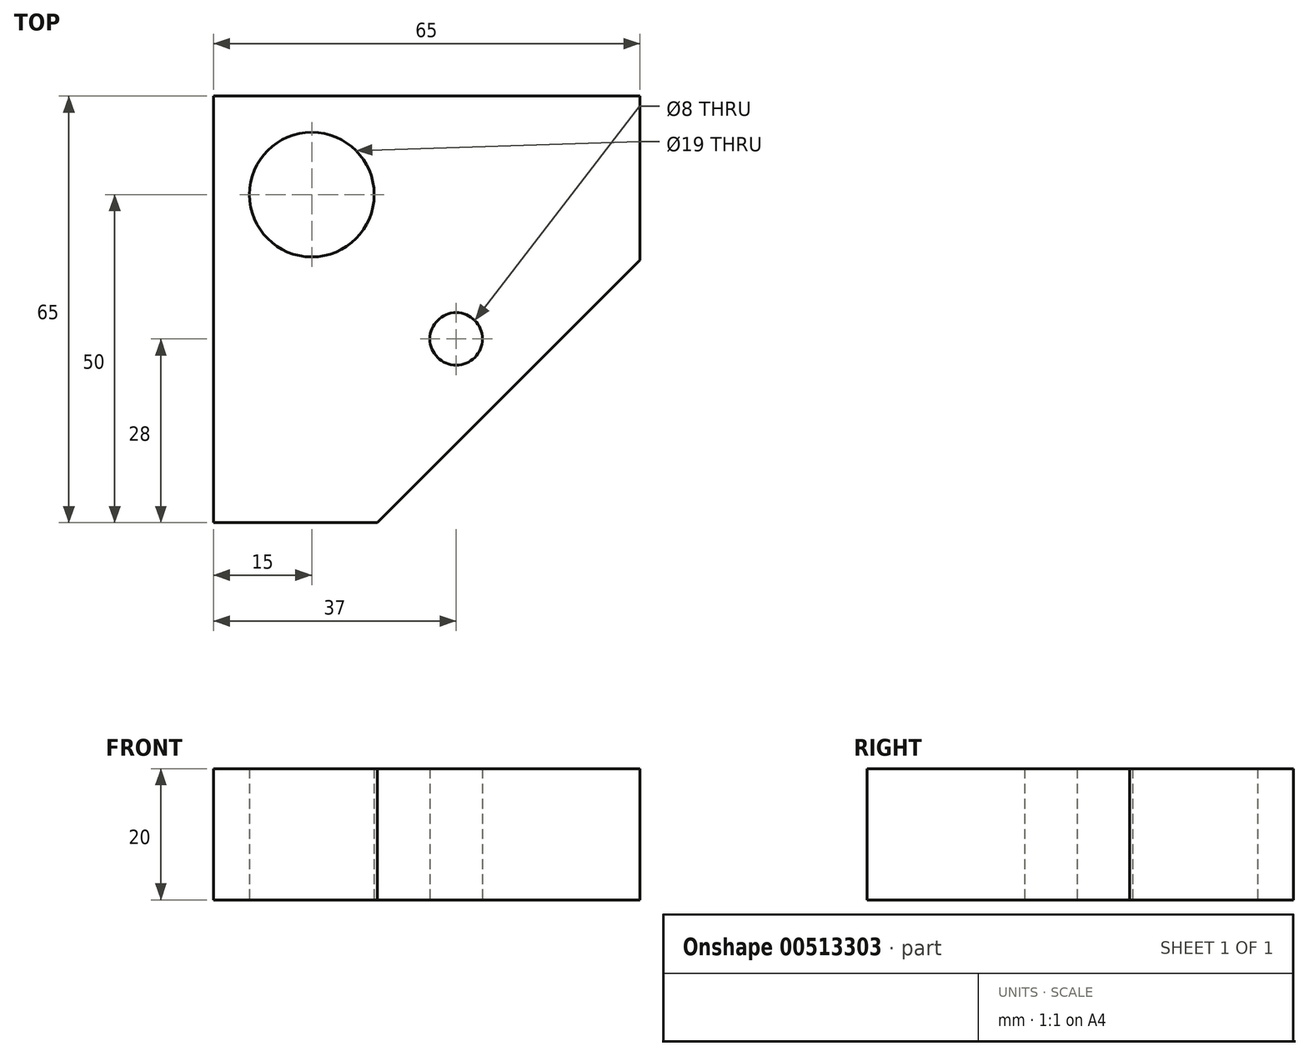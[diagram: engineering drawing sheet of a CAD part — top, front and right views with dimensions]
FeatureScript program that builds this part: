
annotation { "Feature Type Name" : "Feature", "Feature Type Description" : "" }
export const myFeature = defineFeature(function(context is Context, id is Id, definition is map)
    precondition{}
    {
        {
            var Q0;
            Q0=qCreatedBy(makeId("Top.planeOp"),FACE);
            var sketch = newSketch(context, id + "F0", { "sketchPlane" : qUnion([Q0])});
            skCircle(sketch, "E0", {"center": v(15, -15) * mm, "radius": 9.5 * mm});
            skLineSegment(sketch, "E1", {"start": v(25, -65) * mm, "end": v(0, -65) * mm});
            skLineSegment(sketch, "E2", {"start": v(65, -25) * mm, "end": v(65, 0) * mm});
            skLineSegment(sketch, "E3", {"start": v(25, -65) * mm, "end": v(65, -25) * mm});
            skLineSegment(sketch, "E4", {"start": v(0, 0) * mm, "end": v(0, -65) * mm});
            skLineSegment(sketch, "E5", {"start": v(0, 0) * mm, "end": v(65, 0) * mm});
            skLineSegment(sketch, "E6", {"start": v(0, 0) * mm, "end": v(45, -45) * mm});
            skCircle(sketch, "E7", {"center": v(37, -37) * mm, "radius": 4 * mm});
            skSolve(sketch);
        }
        {
            var Q0;
            Q0 = qSketchRegion(id + "F0", true);
            extrude(context, id + "F1", {"entities" : qUnion([Q0]), "depth" : 20 * mm, "offsetDistance" : 25 * mm});
        }
    });
